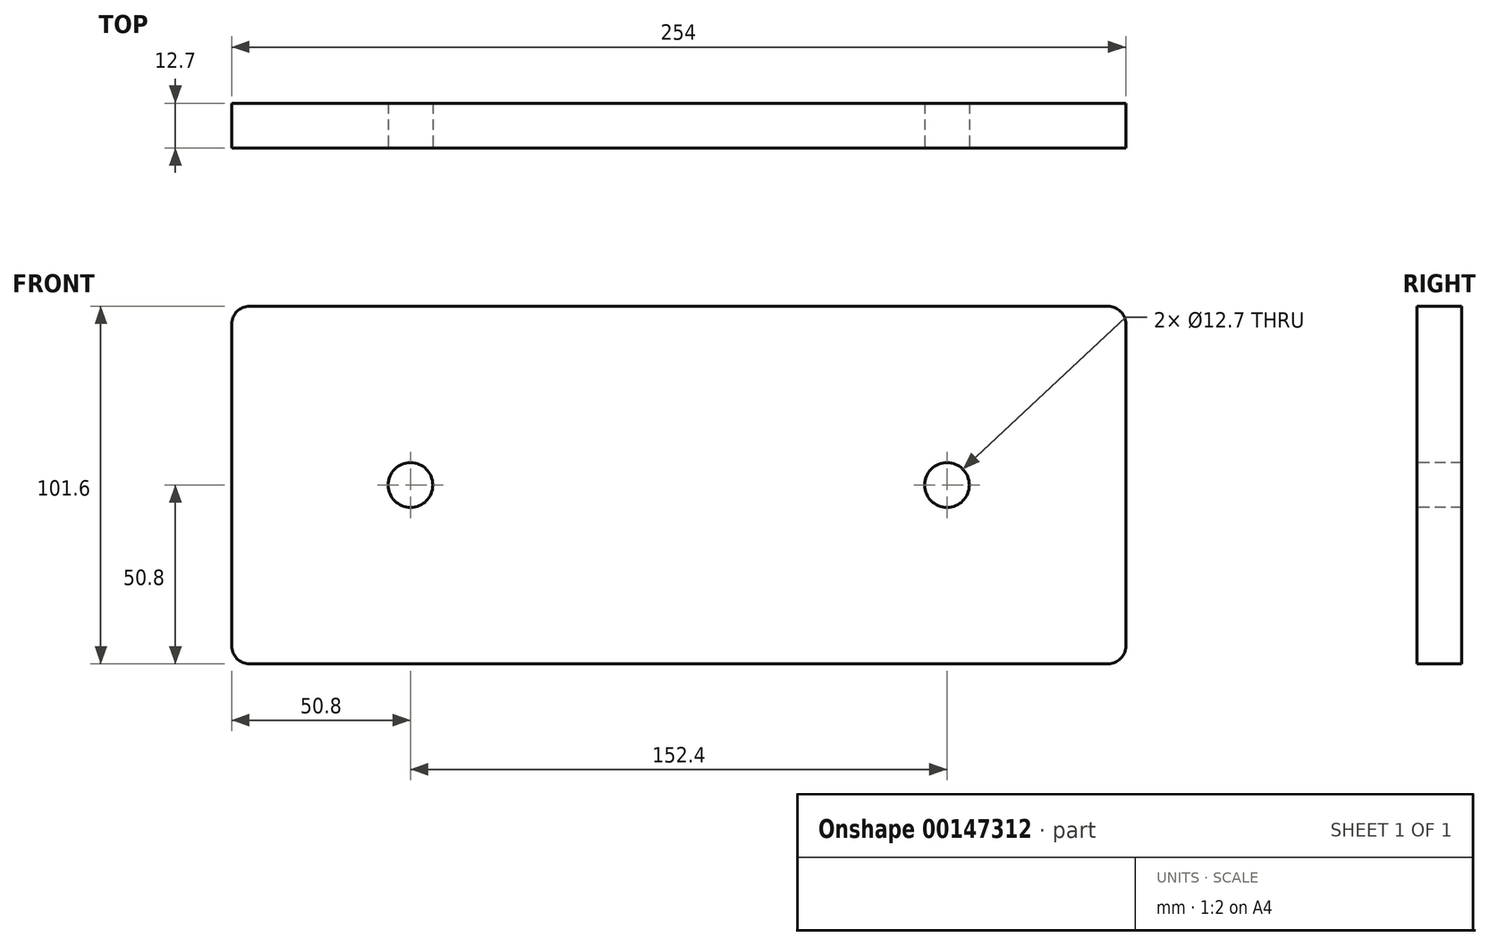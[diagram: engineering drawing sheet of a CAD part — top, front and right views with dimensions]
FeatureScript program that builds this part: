
annotation { "Feature Type Name" : "Feature", "Feature Type Description" : "" }
export const myFeature = defineFeature(function(context is Context, id is Id, definition is map)
    precondition{}
    {
        {
            var Q0;
            Q0=qCreatedBy(makeId("Front.planeOp"),FACE);
            var sketch = newSketch(context, id + "F0", { "sketchPlane" : qUnion([Q0])});
            skLineSegment(sketch, "E0.bottom", {"start": v(0, 0) * mm, "end": v(-254, 0) * mm});
            skLineSegment(sketch, "E0.top", {"start": v(0, 101.6) * mm, "end": v(-254, 101.6) * mm});
            skLineSegment(sketch, "E0.left", {"start": v(0, 0) * mm, "end": v(0, 101.6) * mm});
            skLineSegment(sketch, "E0.right", {"start": v(-254, 0) * mm, "end": v(-254, 101.6) * mm});
            skPoint(sketch, "E1", {"position": v(-33.04, 50.8) * mm});
            skPoint(sketch, "E1.positionSnap0", {"position": v(0, 50.8) * mm});
            skPoint(sketch, "E2", {"position": v(-217.55, 50.8) * mm});
            skPoint(sketch, "E2.positionSnap0", {"position": v(-254, 50.8) * mm});
            skSolve(sketch);
        }
        {
            var Q0;
            Q0=makeQuery(id+"F0.imprint","IMPRINT",FACE,{"disambiguationData":[TD([[makeQuery(id+"F0.imprint","IMPRINT",EDGE,{"derivedFrom":sQuery(id+"F0.wireOp",EDGE,"E0.bottom")}),-1.0]])]});
            extrude(context, id + "F1", {"entities" : qUnion([Q0]), "depth" : 12.7 * mm});
        }
        {
            var Q0;
            Q0=makeQuery(id+"F1.opExtrude","CAP_FACE",FACE,{"disambiguationData":[OSD([sQuery(id+"F0.wireOp",EDGE,"E0.bottom"),sQuery(id+"F0.wireOp",EDGE,"E0.top"),sQuery(id+"F0.wireOp",EDGE,"E0.left"),sQuery(id+"F0.wireOp",EDGE,"E0.right")])],"isStart":false});
            var sketch = newSketch(context, id + "F2", { "sketchPlane" : qUnion([Q0])});
            skCircle(sketch, "E3", {"center": v(-203.2, 50.8) * mm, "radius": 6.35 * mm});
            skCircle(sketch, "E4", {"center": v(-50.8, 50.8) * mm, "radius": 6.35 * mm});
            skSolve(sketch);
        }
        {
            var Q0;
            Q0 = qSketchRegion(id + "F2", true);
            extrude(context, id + "F3", {"entities" : qUnion([Q0]), "operationType" : NewBodyOperationType.REMOVE, "endBound" : BoundingType.THROUGH_ALL, "oppositeDirection" : true, "depth" : 25.4 * mm});
        }
        {
            var Q0;
            Q0=makeQuery(id+"F1.opExtrude","SWEPT_EDGE",EDGE,{"disambiguationData":[OSD([sQuery(id+"F0.wireOp",EDGE,"E0.bottom"),sQuery(id+"F0.wireOp",EDGE,"E0.right")])]});
            var Q1;
            Q1=makeQuery(id+"F1.opExtrude","SWEPT_EDGE",EDGE,{"disambiguationData":[OSD([sQuery(id+"F0.wireOp",EDGE,"E0.top"),sQuery(id+"F0.wireOp",EDGE,"E0.right")])]});
            var Q2;
            Q2=makeQuery(id+"F1.opExtrude","SWEPT_EDGE",EDGE,{"disambiguationData":[OSD([sQuery(id+"F0.wireOp",EDGE,"E0.bottom"),sQuery(id+"F0.wireOp",EDGE,"E0.left")])]});
            var Q3;
            Q3=makeQuery(id+"F1.opExtrude","SWEPT_EDGE",EDGE,{"disambiguationData":[OSD([sQuery(id+"F0.wireOp",EDGE,"E0.top"),sQuery(id+"F0.wireOp",EDGE,"E0.left")])]});
            fillet(context, id + "F4", {"entities" : qUnion([Q0, Q1, Q2, Q3]), "radius" : 5.08 * mm, "tangentPropagation" : true, "allowEdgeOverflow" : false});
        }
    });
